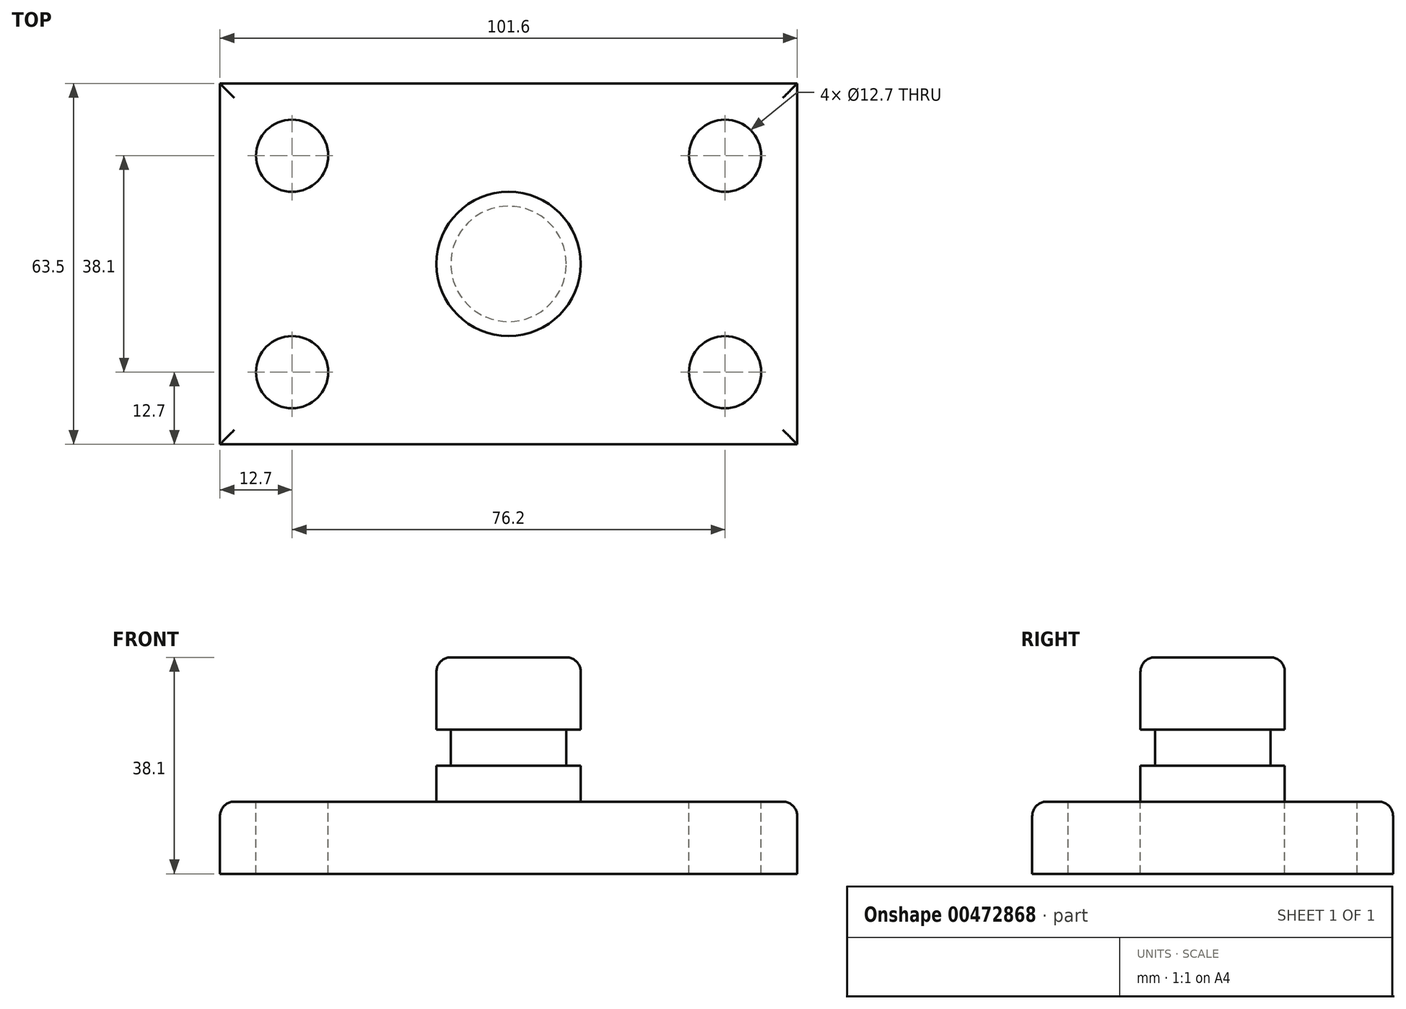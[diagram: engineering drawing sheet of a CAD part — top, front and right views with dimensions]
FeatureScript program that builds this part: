
annotation { "Feature Type Name" : "Feature", "Feature Type Description" : "" }
export const myFeature = defineFeature(function(context is Context, id is Id, definition is map)
    precondition{}
    {
        {
            var Q0;
            Q0=qCreatedBy(makeId("Top.planeOp"),FACE);
            var sketch = newSketch(context, id + "F0", { "sketchPlane" : qUnion([Q0])});
            skLineSegment(sketch, "E0.bottom", {"start": v(50.8, 31.75) * mm, "end": v(-50.8, 31.75) * mm});
            skLineSegment(sketch, "E0.top", {"start": v(50.8, -31.75) * mm, "end": v(-50.8, -31.75) * mm});
            skLineSegment(sketch, "E0.left", {"start": v(50.8, 31.75) * mm, "end": v(50.8, -31.75) * mm});
            skLineSegment(sketch, "E0.right", {"start": v(-50.8, 31.75) * mm, "end": v(-50.8, -31.75) * mm});
            skPoint(sketch, "E0.middle", {"position": v(0, 0) * mm});
            skSolve(sketch);
        }
        {
            var Q0;
            Q0=makeQuery(id+"F0.imprint","IMPRINT",FACE,{"disambiguationData":[TD([[makeQuery(id+"F0.imprint","IMPRINT",EDGE,{"derivedFrom":sQuery(id+"F0.wireOp",EDGE,"E0.bottom")}),1.0]])]});
            extrude(context, id + "F1", {"entities" : qUnion([Q0]), "depth" : 12.7 * mm});
        }
        {
            var Q0;
            Q0=makeQuery(id+"F1.opExtrude","CAP_FACE",FACE,{"disambiguationData":[OSD([sQuery(id+"F0.wireOp",EDGE,"E0.bottom"),sQuery(id+"F0.wireOp",EDGE,"E0.top"),sQuery(id+"F0.wireOp",EDGE,"E0.left"),sQuery(id+"F0.wireOp",EDGE,"E0.right")])],"isStart":false});
            var sketch = newSketch(context, id + "F2", { "sketchPlane" : qUnion([Q0])});
            skCircle(sketch, "E1", {"center": v(-38.1, 19.05) * mm, "radius": 6.35 * mm});
            skCircle(sketch, "E2", {"center": v(38.1, 19.05) * mm, "radius": 6.35 * mm});
            skCircle(sketch, "E3", {"center": v(38.1, -19.05) * mm, "radius": 6.35 * mm});
            skCircle(sketch, "E4", {"center": v(-38.1, -19.05) * mm, "radius": 6.35 * mm});
            skSolve(sketch);
        }
        {
            var Q0;
            Q0=makeQuery(id+"F2.imprint","IMPRINT",FACE,{"disambiguationData":[TD([[makeQuery(id+"F2.imprint","IMPRINT",EDGE,{"derivedFrom":sQuery(id+"F2.wireOp",EDGE,"E4")}),1.0]])]});
            var Q1;
            Q1=makeQuery(id+"F2.imprint","IMPRINT",FACE,{"disambiguationData":[TD([[makeQuery(id+"F2.imprint","IMPRINT",EDGE,{"derivedFrom":sQuery(id+"F2.wireOp",EDGE,"E1")}),1.0]])]});
            var Q2;
            Q2=makeQuery(id+"F2.imprint","IMPRINT",FACE,{"disambiguationData":[TD([[makeQuery(id+"F2.imprint","IMPRINT",EDGE,{"derivedFrom":sQuery(id+"F2.wireOp",EDGE,"E2")}),1.0]])]});
            var Q3;
            Q3=makeQuery(id+"F2.imprint","IMPRINT",FACE,{"disambiguationData":[TD([[makeQuery(id+"F2.imprint","IMPRINT",EDGE,{"derivedFrom":sQuery(id+"F2.wireOp",EDGE,"E3")}),1.0]])]});
            extrude(context, id + "F3", {"entities" : qUnion([Q0, Q1, Q2, Q3]), "operationType" : NewBodyOperationType.REMOVE, "endBound" : BoundingType.THROUGH_ALL, "oppositeDirection" : true, "depth" : 25.4 * mm});
        }
        {
            var Q0;
            Q0=qCreatedBy(makeId("Front.planeOp"),FACE);
            var sketch = newSketch(context, id + "F4", { "sketchPlane" : qUnion([Q0])});
            skLineSegment(sketch, "E5.bottom", {"start": v(0, 12.7) * mm, "end": v(12.7, 12.7) * mm});
            skLineSegment(sketch, "E5.top", {"start": v(0, 38.1) * mm, "end": v(12.7, 38.1) * mm});
            skLineSegment(sketch, "E5.left", {"start": v(0, 12.7) * mm, "end": v(0, 38.1) * mm});
            skLineSegment(sketch, "E5.right", {"start": v(12.7, 12.7) * mm, "end": v(12.7, 38.1) * mm});
            skSolve(sketch);
        }
        {
            var Q0;
            Q0=makeQuery(id+"F4.imprint","IMPRINT",FACE,{"disambiguationData":[TD([[makeQuery(id+"F4.imprint","IMPRINT",EDGE,{"derivedFrom":sQuery(id+"F4.wireOp",EDGE,"E5.bottom")}),1.0]])]});
            var Q1;
            Q1=sQuery(id+"F4.wireOp",EDGE,"E5.left");
            revolve(context, id + "F5", {"operationType" : NewBodyOperationType.ADD, "entities" : qUnion([Q0]), "axis" : qUnion([Q1]), "revolveType" : RevolveType.FULL});
        }
        {
            var Q0;
            Q0=qCreatedBy(makeId("Front.planeOp"),FACE);
            var sketch = newSketch(context, id + "F6", { "sketchPlane" : qUnion([Q0])});
            skLineSegment(sketch, "E6.bottom", {"start": v(17.78, 25.4) * mm, "end": v(10.16, 25.4) * mm});
            skLineSegment(sketch, "E6.top", {"start": v(17.78, 19.05) * mm, "end": v(10.16, 19.05) * mm});
            skLineSegment(sketch, "E6.left", {"start": v(17.78, 25.4) * mm, "end": v(17.78, 19.05) * mm});
            skLineSegment(sketch, "E6.right", {"start": v(10.16, 25.4) * mm, "end": v(10.16, 19.05) * mm});
            skSolve(sketch);
        }
        {
            var Q0;
            Q0=makeQuery(id+"F6.imprint","IMPRINT",FACE,{"disambiguationData":[TD([[makeQuery(id+"F6.imprint","IMPRINT",EDGE,{"derivedFrom":sQuery(id+"F6.wireOp",EDGE,"E6.bottom")}),1.0]])]});
            var Q1;
            Q1=makeQuery(id+"F5.opRevolve","SWEPT_FACE",FACE,{"disambiguationData":[OSD([sQuery(id+"F4.wireOp",EDGE,"E5.right")])]});
            revolve(context, id + "F7", {"operationType" : NewBodyOperationType.REMOVE, "entities" : qUnion([Q0]), "axis" : qUnion([Q1]), "revolveType" : RevolveType.FULL, "oppositeDirection" : true});
        }
        {
            var Q0;
            Q0=makeQuery(id+"F1.opExtrude","CAP_EDGE",EDGE,{"disambiguationData":[OSD([sQuery(id+"F0.wireOp",EDGE,"E0.bottom")])],"isStart":false});
            var Q1;
            Q1=makeQuery(id+"F1.opExtrude","CAP_EDGE",EDGE,{"disambiguationData":[OSD([sQuery(id+"F0.wireOp",EDGE,"E0.top")])],"isStart":false});
            var Q2;
            Q2=makeQuery(id+"F1.opExtrude","CAP_EDGE",EDGE,{"disambiguationData":[OSD([sQuery(id+"F0.wireOp",EDGE,"E0.right")])],"isStart":false});
            var Q3;
            Q3=makeQuery(id+"F1.opExtrude","CAP_EDGE",EDGE,{"disambiguationData":[OSD([sQuery(id+"F0.wireOp",EDGE,"E0.left")])],"isStart":false});
            fillet(context, id + "F8", {"entities" : qUnion([Q0, Q1, Q2, Q3]), "radius" : 2.54 * mm, "tangentPropagation" : true, "allowEdgeOverflow" : false});
        }
        {
            var Q0;
            Q0=makeQuery(id+"F5.opRevolve","SWEPT_EDGE",EDGE,{"disambiguationData":[OSD([sQuery(id+"F4.wireOp",EDGE,"E5.bottom"),sQuery(id+"F4.wireOp",EDGE,"E5.right")])]});
            var Q1;
            Q1=makeQuery(id+"F5.opRevolve","SWEPT_EDGE",EDGE,{"disambiguationData":[OSD([sQuery(id+"F4.wireOp",EDGE,"E5.top"),sQuery(id+"F4.wireOp",EDGE,"E5.right")])]});
            fillet(context, id + "F9", {"entities" : qUnion([Q0, Q1]), "radius" : 2.54 * mm, "tangentPropagation" : true, "allowEdgeOverflow" : false});
        }
    });
